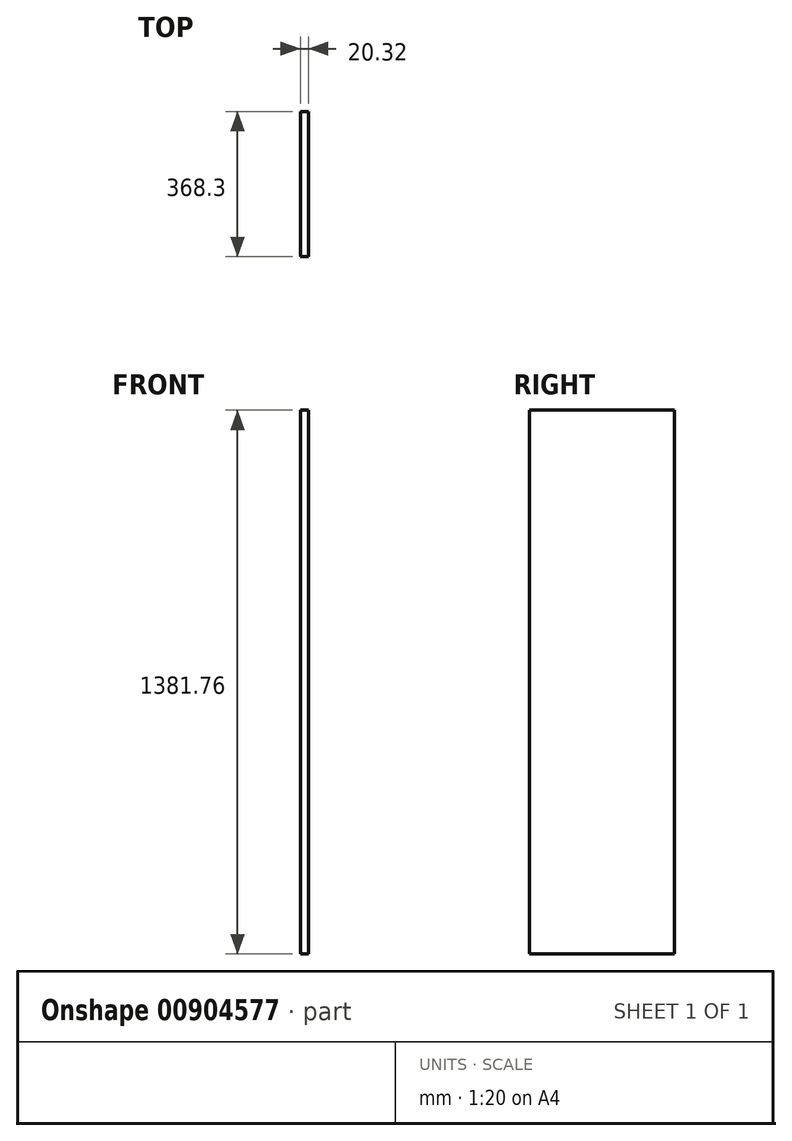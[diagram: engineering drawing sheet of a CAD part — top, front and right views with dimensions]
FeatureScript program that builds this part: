
annotation { "Feature Type Name" : "Feature", "Feature Type Description" : "" }
export const myFeature = defineFeature(function(context is Context, id is Id, definition is map)
    precondition{}
    {
        {
            var Q0;
            Q0=qCreatedBy(makeId("Right.planeOp"),FACE);
            var sketch = newSketch(context, id + "F0", { "sketchPlane" : qUnion([Q0])});
            skLineSegment(sketch, "E0.bottom", {"start": v(-184.15, 690.88) * mm, "end": v(184.15, 690.88) * mm});
            skLineSegment(sketch, "E0.top", {"start": v(-184.15, -690.88) * mm, "end": v(184.15, -690.88) * mm});
            skLineSegment(sketch, "E0.left", {"start": v(-184.15, 690.88) * mm, "end": v(-184.15, -690.88) * mm});
            skLineSegment(sketch, "E0.right", {"start": v(184.15, 690.88) * mm, "end": v(184.15, -690.88) * mm});
            skPoint(sketch, "E0.middle", {"position": v(0, 0) * mm});
            skSolve(sketch);
        }
        {
            var Q0;
            Q0=makeQuery(id+"F0.imprint","IMPRINT",FACE,{"disambiguationData":[TD([[makeQuery(id+"F0.imprint","IMPRINT",EDGE,{"derivedFrom":sQuery(id+"F0.wireOp",EDGE,"E0.bottom")}),-1.0]])]});
            extrude(context, id + "F1", {"entities" : qUnion([Q0]), "depth" : 20.32 * mm, "offsetDistance" : 25.4 * mm});
        }
    });
